# Revit family: Sanitary_Taps-Mixers_hansgrohe_72481XXX-Rebris-E-2-hole-rim-mounted-bat_NEW
name_source: partatom
category: Plumbing Fixtures
revit_build: Autodesk Revit 2018 (Build: 20170223_1515(x64)
units: mm (PartAtom-declared; Revit-internal decimal feet)

## family parameters
Always vertical = No
Cut with Voids When Loaded = No
OmniClass Number = 23.31.11.00
OmniClass Title = Faucets
Part Type = Normal
Room Calculation Point = No
Round Connector Dimension = Use Diameter
Shared = No
Work Plane-Based = Yes

## types (2) — shared parameters
Always visible = Yes
BIMobject category = Taps & Mixers
Connector Description = Water Inlet 19.1mm
Default Elevation = 1219 mm
Description = Rebris E 2-hole rim mounted bath mixer with diverter valve and Vernis Blend hand shower Vario
Design country = Germany
Diameter = 19 mm
Edition number = 1
IFC Classification = Valve
Manufacturer = Hansgrohe
Manufacturer country = Germany
Manufacturer name = hansgrohe
Masterformat 2014 Code = 22 41 39
Masterformat 2014 Description = Residential Faucets, Supplies, and Trim
Material 2 = Hansgrohe - Plastic - White
Model = 72481XXX
OmniClass Code = 23-31 11 00
OmniClass Description = Faucets
Product Guid = acab4b4e-77b3-44a4-8ff4-8d2aac467b63
Product SKU = 72481XXX
Product data url = https://bimobject.com
Product family = Rebris E
Product group = Bath mixers
Product name = 72481XXX Rebris E 2-hole rim mounted bath mixer with diverter valve and Vernis Blend hand shower Vario
Product url = https://www.hansgrohe.com
QR code = https://bimobject.com
UNSPSC Code = 301815
URL = https://www.hansgrohe.com
Uniclass 2015 Code = Pr_40_20_87
Uniclass 2015 Name = Taps and water supply outlet fittings
Uniformat II Code = D2010
Uniformat II Description = Plumbing Fixtures
Weight Net (Kg) = 2.5

## per-type parameters (varying)
| type | Material 1 |
| 670 Matte Black | Hansgrohe - Metal - 670 Matte Black |
| 000 Chrome | Hansgrohe - Metal - 000 Chrome |

## geometry (parser evidence)
native form markers: Blend x9, Sweep x2
no freeform markers — native parametric forms only
